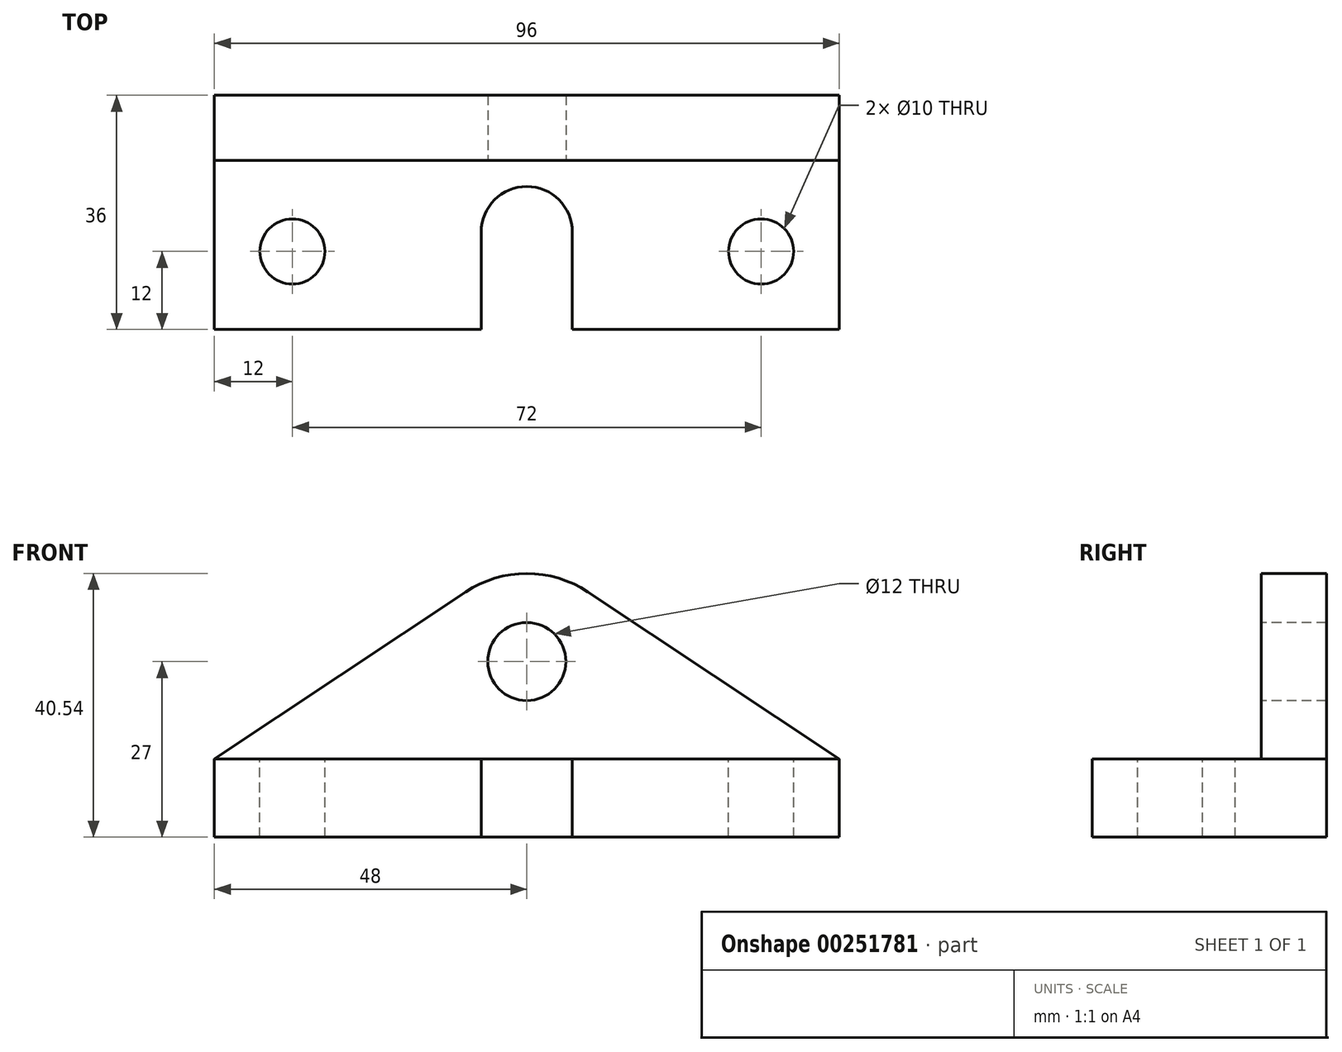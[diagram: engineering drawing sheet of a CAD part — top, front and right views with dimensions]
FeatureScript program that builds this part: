
annotation { "Feature Type Name" : "Feature", "Feature Type Description" : "" }
export const myFeature = defineFeature(function(context is Context, id is Id, definition is map)
    precondition{}
    {
        {
            var Q0;
            Q0=qCreatedBy(makeId("Front.planeOp"),FACE);
            var sketch = newSketch(context, id + "F0", { "sketchPlane" : qUnion([Q0])});
            skLineSegment(sketch, "E0.bottom", {"start": v(-48, 6) * mm, "end": v(48, 6) * mm});
            skLineSegment(sketch, "E0.top", {"start": v(-48, -6) * mm, "end": v(48, -6) * mm});
            skLineSegment(sketch, "E0.left", {"start": v(-48, 6) * mm, "end": v(-48, -6) * mm});
            skLineSegment(sketch, "E0.right", {"start": v(48, 6) * mm, "end": v(48, -6) * mm});
            skPoint(sketch, "E0.middle", {"position": v(0, 0) * mm});
            skSolve(sketch);
        }
        {
            var Q0;
            Q0 = qSketchRegion(id + "F0", true);
            extrude(context, id + "F1", {"entities" : qUnion([Q0]), "endBound" : BoundingType.SYMMETRIC, "oppositeDirection" : true, "depth" : 36 * mm});
        }
        {
            var Q0;
            Q0=makeQuery(id+"F1.opExtrude","CAP_FACE",FACE,{"disambiguationData":[OSD([sQuery(id+"F0.wireOp",EDGE,"E0.bottom"),sQuery(id+"F0.wireOp",EDGE,"E0.top"),sQuery(id+"F0.wireOp",EDGE,"E0.left"),sQuery(id+"F0.wireOp",EDGE,"E0.right")])],"isStart":false});
            var sketch = newSketch(context, id + "F2", { "sketchPlane" : qUnion([Q0])});
            skLineSegment(sketch, "E1", {"start": v(-48, 6) * mm, "end": v(0, 37.96) * mm});
            skLineSegment(sketch, "E2", {"start": v(0, 37.96) * mm, "end": v(48, 6) * mm});
            skLineSegment(sketch, "E3.0", {"start": v(48, 6) * mm, "end": v(-48, 6) * mm});
            skSolve(sketch);
        }
        {
            var Q0;
            Q0 = qSketchRegion(id + "F2", true);
            extrude(context, id + "F3", {"entities" : qUnion([Q0]), "operationType" : NewBodyOperationType.ADD, "oppositeDirection" : true, "depth" : 10 * mm});
        }
        {
            var Q0;
            Q0=makeQuery(id+"F3.opExtrude","SWEPT_EDGE",EDGE,{"disambiguationData":[OSD([sQuery(id+"F2.wireOp",EDGE,"E1"),sQuery(id+"F2.wireOp",EDGE,"E2")])]});
            fillet(context, id + "F4", {"entities" : qUnion([Q0]), "radius" : 17 * mm, "tangentPropagation" : true, "allowEdgeOverflow" : false});
        }
        {
            var Q0;
            Q0=makeQuery(id+"F3.opExtrude","CAP_FACE",FACE,{"disambiguationData":[OSD([sQuery(id+"F2.wireOp",EDGE,"E1"),sQuery(id+"F2.wireOp",EDGE,"E2"),sQuery(id+"F2.wireOp",EDGE,"E3.0")])],"isStart":false});
            var sketch = newSketch(context, id + "F5", { "sketchPlane" : qUnion([Q0])});
            skCircle(sketch, "E4", {"center": v(0, 21) * mm, "radius": 6 * mm});
            skPoint(sketch, "E4.centerSnap0", {"position": v(0, 34.54) * mm});
            skSolve(sketch);
        }
        {
            var Q0;
            Q0 = qSketchRegion(id + "F5", true);
            extrude(context, id + "F6", {"entities" : qUnion([Q0]), "operationType" : NewBodyOperationType.REMOVE, "endBound" : BoundingType.THROUGH_ALL, "oppositeDirection" : true, "depth" : 25 * mm});
        }
        {
            var Q0;
            Q0=makeQuery(id+"F1.opExtrude","SWEPT_FACE",FACE,{"disambiguationData":[OSD([sQuery(id+"F0.wireOp",EDGE,"E0.bottom")])]});
            var sketch = newSketch(context, id + "F7", { "sketchPlane" : qUnion([Q0])});
            skLineSegment(sketch, "E5.bottom", {"start": v(7, -3) * mm, "end": v(-7, -3) * mm});
            skLineSegment(sketch, "E5.top", {"start": v(7, -33) * mm, "end": v(-7, -33) * mm});
            skLineSegment(sketch, "E5.left", {"start": v(7, -3) * mm, "end": v(7, -33) * mm});
            skLineSegment(sketch, "E5.right", {"start": v(-7, -3) * mm, "end": v(-7, -33) * mm});
            skPoint(sketch, "E5.middle", {"position": v(0, -18) * mm});
            skLineSegment(sketch, "E6.0", {"start": v(-48, -18) * mm, "end": v(48, -18) * mm});
            skSolve(sketch);
        }
        {
            var Q0;
            Q0 = qSketchRegion(id + "F7", true);
            extrude(context, id + "F8", {"entities" : qUnion([Q0]), "operationType" : NewBodyOperationType.REMOVE, "oppositeDirection" : true, "depth" : 25 * mm});
        }
        {
            var Q0;
            Q0=makeQuery(id+"F1.opExtrude","SWEPT_FACE",FACE,{"disambiguationData":[OSD([sQuery(id+"F0.wireOp",EDGE,"E0.bottom")])]});
            var sketch = newSketch(context, id + "F9", { "sketchPlane" : qUnion([Q0])});
            skCircle(sketch, "E7", {"center": v(0, -3) * mm, "radius": 7 * mm});
            skSolve(sketch);
        }
        {
            var Q0;
            Q0 = qSketchRegion(id + "F9", true);
            extrude(context, id + "F10", {"entities" : qUnion([Q0]), "operationType" : NewBodyOperationType.REMOVE, "oppositeDirection" : true, "depth" : 25 * mm});
        }
        {
            var Q0;
            Q0=makeQuery(id+"F1.opExtrude","SWEPT_FACE",FACE,{"disambiguationData":[OSD([sQuery(id+"F0.wireOp",EDGE,"E0.bottom")])]});
            var sketch = newSketch(context, id + "F11", { "sketchPlane" : qUnion([Q0])});
            skPoint(sketch, "E8.centerSnap0", {"position": v(48, -5) * mm});
            skCircle(sketch, "E9", {"center": v(36, -6) * mm, "radius": 5 * mm});
            skCircle(sketch, "E10", {"center": v(-36, -6) * mm, "radius": 5 * mm});
            skSolve(sketch);
        }
        {
            var Q0;
            Q0 = qSketchRegion(id + "F11", true);
            extrude(context, id + "F12", {"entities" : qUnion([Q0]), "operationType" : NewBodyOperationType.REMOVE, "endBound" : BoundingType.THROUGH_ALL, "oppositeDirection" : true, "depth" : 25 * mm});
        }
    });
